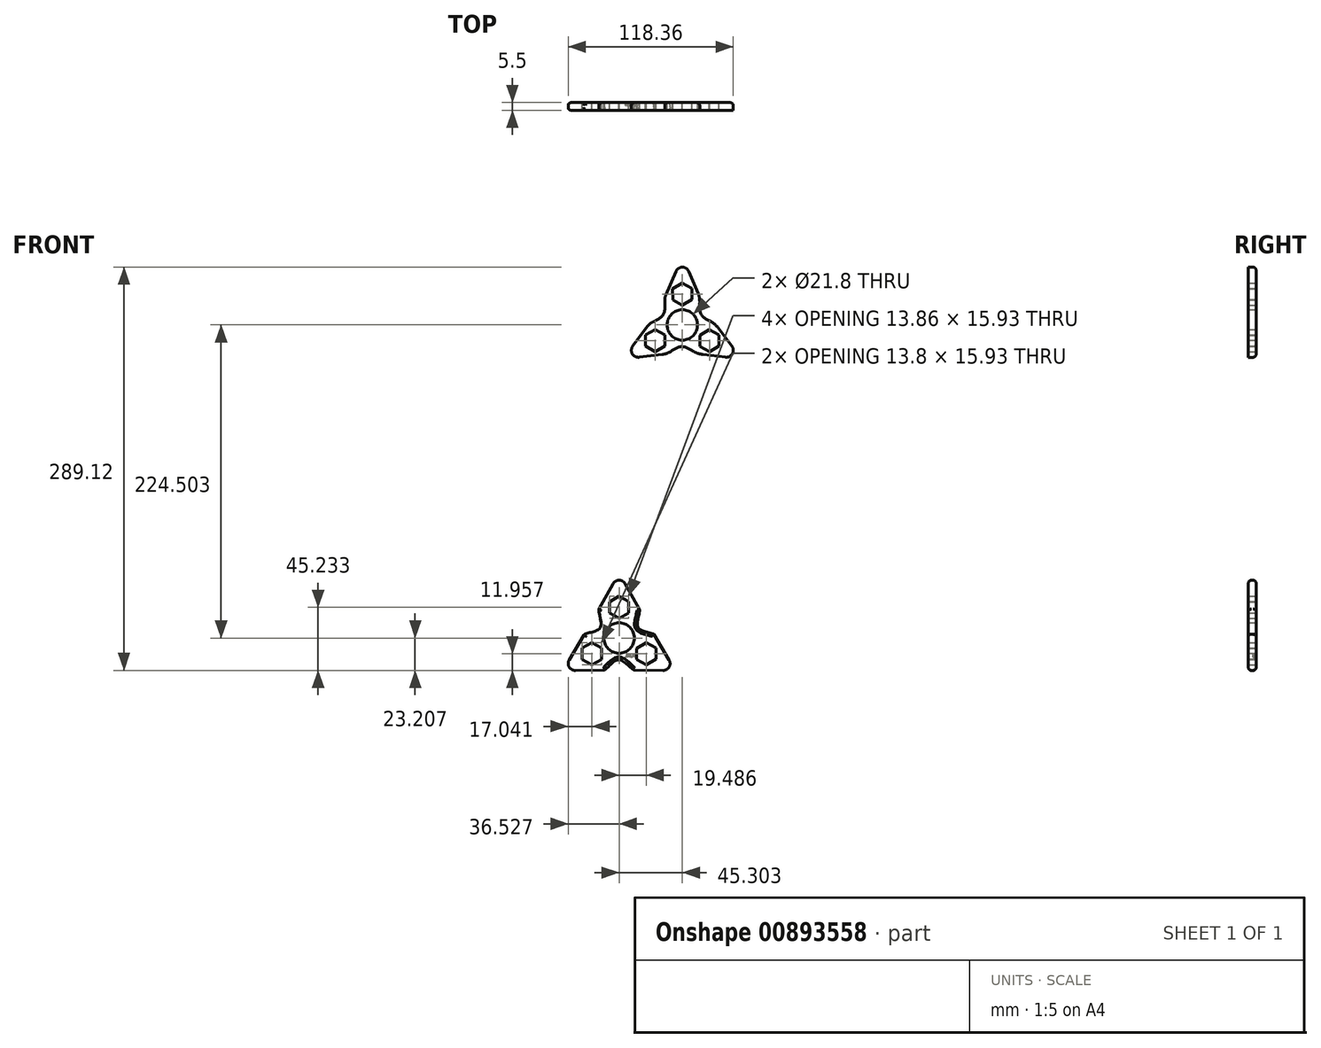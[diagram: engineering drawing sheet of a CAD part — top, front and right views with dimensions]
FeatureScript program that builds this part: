
annotation { "Feature Type Name" : "Feature", "Feature Type Description" : "" }
export const myFeature = defineFeature(function(context is Context, id is Id, definition is map)
    precondition{}
    {
        {
            var Q0;
            Q0=qCreatedBy(makeId("Front.planeOp"),FACE);
            var sketch = newSketch(context, id + "F0", { "sketchPlane" : qUnion([Q0])});
            skCircle(sketch, "E0", {"center": v(0, 0) * mm, "radius": 10.9 * mm});
            skCircle(sketch, "E1.cCircle", {"center": v(0, 22.03) * mm, "radius": 6.9 * mm, "construction": true});
            skLineSegment(sketch, "E1.0", {"start": v(0.06, 14.06) * mm, "end": v(-6.87, 17.99) * mm});
            skLineSegment(sketch, "E1.1", {"start": v(-6.87, 17.99) * mm, "end": v(-6.93, 25.96) * mm});
            skLineSegment(sketch, "E1.2", {"start": v(-6.93, 25.96) * mm, "end": v(-0.06, 30) * mm});
            skLineSegment(sketch, "E1.3", {"start": v(-0.06, 30) * mm, "end": v(6.87, 26.06) * mm});
            skLineSegment(sketch, "E1.4", {"start": v(6.87, 26.06) * mm, "end": v(6.93, 18.1) * mm});
            skLineSegment(sketch, "E1.5", {"start": v(6.93, 18.1) * mm, "end": v(0.06, 14.06) * mm});
            skLineSegment(sketch, "E2", {"start": v(0, 10.9) * mm, "end": v(0.06, 14.06) * mm});
            skCircle(sketch, "E3.cCircle", {"center": v(-19.49, -11.25) * mm, "radius": 6.9 * mm, "construction": true});
            skLineSegment(sketch, "E3.0", {"start": v(-26.39, -15.23) * mm, "end": v(-26.39, -7.27) * mm});
            skLineSegment(sketch, "E3.1", {"start": v(-26.39, -7.27) * mm, "end": v(-19.49, -3.28) * mm});
            skLineSegment(sketch, "E3.2", {"start": v(-19.49, -3.28) * mm, "end": v(-12.59, -7.27) * mm});
            skLineSegment(sketch, "E3.3", {"start": v(-12.59, -7.27) * mm, "end": v(-12.59, -15.23) * mm});
            skLineSegment(sketch, "E3.4", {"start": v(-12.59, -15.23) * mm, "end": v(-19.49, -19.22) * mm});
            skLineSegment(sketch, "E3.5", {"start": v(-19.49, -19.22) * mm, "end": v(-26.39, -15.23) * mm});
            skPoint(sketch, "E3.0.midPoint", {"position": v(-26.39, -11.25) * mm});
            skCircle(sketch, "E4.cCircle", {"center": v(19.49, -11.25) * mm, "radius": 6.9 * mm, "construction": true});
            skLineSegment(sketch, "E4.0", {"start": v(19.42, -3.28) * mm, "end": v(26.35, -7.21) * mm});
            skLineSegment(sketch, "E4.1", {"start": v(26.35, -7.21) * mm, "end": v(26.42, -15.18) * mm});
            skLineSegment(sketch, "E4.2", {"start": v(26.42, -15.18) * mm, "end": v(19.55, -19.22) * mm});
            skLineSegment(sketch, "E4.3", {"start": v(19.55, -19.22) * mm, "end": v(12.62, -15.29) * mm});
            skLineSegment(sketch, "E4.4", {"start": v(12.62, -15.29) * mm, "end": v(12.56, -7.32) * mm});
            skLineSegment(sketch, "E4.5", {"start": v(12.56, -7.32) * mm, "end": v(19.42, -3.28) * mm});
            skPoint(sketch, "E4.0.midPoint", {"position": v(22.89, -5.25) * mm});
            skLineSegment(sketch, "E5", {"start": v(-12.76, 19.17) * mm, "end": v(-4.6, 38.37) * mm});
            skLineSegment(sketch, "E6.MirrorCS", {"start": v(12.76, 19.17) * mm, "end": v(4.6, 38.37) * mm});
            skLineSegment(sketch, "E7.MirrorCS", {"start": v(-10.22, -20.64) * mm, "end": v(-30.92, -23.17) * mm});
            skLineSegment(sketch, "E8.MirrorCS", {"start": v(-22.99, 1.46) * mm, "end": v(-35.53, -15.2) * mm});
            skLineSegment(sketch, "E9.MirrorCS", {"start": v(22.99, 1.46) * mm, "end": v(35.53, -15.2) * mm});
            skLineSegment(sketch, "E10.MirrorCS", {"start": v(10.22, -20.64) * mm, "end": v(30.92, -23.17) * mm});
            skFitSpline(sketch, "E11", {"points": [v(-22.99, 1.46) * mm, v(-13.66, 7.37) * mm, v(-12.76, 19.17) * mm], "startDerivative": vector(23.21, 9.28) * mm, "endDerivative": vector(-2.61, 26.04) * mm});
            skFitSpline(sketch, "E12.MirrorCS", {"points": [v(-10.22, -20.64) * mm, v(-0.44, -15.52) * mm, v(10.22, -20.64) * mm], "startDerivative": vector(19.65, 15.46) * mm, "endDerivative": vector(21.24, -15.28) * mm});
            skFitSpline(sketch, "E13.MirrorCS", {"points": [v(22.99, 1.46) * mm, v(13.66, 7.37) * mm, v(12.76, 19.17) * mm], "startDerivative": vector(-23.21, 9.28) * mm, "endDerivative": vector(2.61, 26.04) * mm});
            skPoint(sketch, "E14.visualSharp", {"position": v(0, 49.19) * mm});
            skArc(sketch, "E14.filletArc", {"start": v(4.6, 38.37) * mm, "mid": v(0, 41.4) * mm, "end": v(-4.6, 38.37) * mm});
            skPoint(sketch, "E15.visualSharp", {"position": v(-42.6, -24.6) * mm});
            skArc(sketch, "E15.filletArc", {"start": v(-35.53, -15.2) * mm, "mid": v(-35.86, -20.7) * mm, "end": v(-30.92, -23.17) * mm});
            skPoint(sketch, "E16.visualSharp", {"position": v(42.6, -24.6) * mm});
            skArc(sketch, "E16.filletArc", {"start": v(30.92, -23.17) * mm, "mid": v(35.86, -20.7) * mm, "end": v(35.53, -15.2) * mm});
            skCircle(sketch, "E17", {"center": v(-45.3, -224.5) * mm, "radius": 10.9 * mm});
            skCircle(sketch, "E18.cCircle", {"center": v(-45.3, -202.48) * mm, "radius": 6.9 * mm, "construction": true});
            skLineSegment(sketch, "E18.0", {"start": v(-45.24, -210.44) * mm, "end": v(-52.17, -206.51) * mm});
            skLineSegment(sketch, "E18.1", {"start": v(-52.17, -206.51) * mm, "end": v(-52.23, -198.55) * mm});
            skLineSegment(sketch, "E18.2", {"start": v(-52.23, -198.55) * mm, "end": v(-45.36, -194.5) * mm});
            skLineSegment(sketch, "E18.3", {"start": v(-45.36, -194.5) * mm, "end": v(-38.43, -198.44) * mm});
            skLineSegment(sketch, "E18.4", {"start": v(-38.43, -198.44) * mm, "end": v(-38.37, -206.4) * mm});
            skLineSegment(sketch, "E18.5", {"start": v(-38.37, -206.4) * mm, "end": v(-45.24, -210.44) * mm});
            skCircle(sketch, "E19.cCircle", {"center": v(-64.79, -235.75) * mm, "radius": 6.9 * mm, "construction": true});
            skLineSegment(sketch, "E19.0", {"start": v(-71.69, -239.74) * mm, "end": v(-71.69, -231.77) * mm});
            skLineSegment(sketch, "E19.1", {"start": v(-71.69, -231.77) * mm, "end": v(-64.79, -227.79) * mm});
            skLineSegment(sketch, "E19.2", {"start": v(-64.79, -227.79) * mm, "end": v(-57.89, -231.77) * mm});
            skLineSegment(sketch, "E19.3", {"start": v(-57.89, -231.77) * mm, "end": v(-57.89, -239.74) * mm});
            skLineSegment(sketch, "E19.4", {"start": v(-57.89, -239.74) * mm, "end": v(-64.79, -243.72) * mm});
            skLineSegment(sketch, "E19.5", {"start": v(-64.79, -243.72) * mm, "end": v(-71.69, -239.74) * mm});
            skPoint(sketch, "E19.0.midPoint", {"position": v(-71.69, -235.75) * mm});
            skCircle(sketch, "E20.cCircle", {"center": v(-25.82, -235.75) * mm, "radius": 6.9 * mm, "construction": true});
            skLineSegment(sketch, "E20.0", {"start": v(-25.88, -227.79) * mm, "end": v(-18.95, -231.72) * mm});
            skLineSegment(sketch, "E20.1", {"start": v(-18.95, -231.72) * mm, "end": v(-18.89, -239.68) * mm});
            skLineSegment(sketch, "E20.2", {"start": v(-18.89, -239.68) * mm, "end": v(-25.76, -243.72) * mm});
            skLineSegment(sketch, "E20.3", {"start": v(-25.76, -243.72) * mm, "end": v(-32.69, -239.79) * mm});
            skLineSegment(sketch, "E20.4", {"start": v(-32.69, -239.79) * mm, "end": v(-32.75, -231.82) * mm});
            skLineSegment(sketch, "E20.5", {"start": v(-32.75, -231.82) * mm, "end": v(-25.88, -227.79) * mm});
            skPoint(sketch, "E20.0.midPoint", {"position": v(-22.41, -229.75) * mm});
            skLineSegment(sketch, "E21.MirrorCS", {"start": v(-20.46, -221.76) * mm, "end": v(-9.48, -240.14) * mm});
            skLineSegment(sketch, "E22.MirrorCS", {"start": v(-34.96, -247.4) * mm, "end": v(-13.85, -247.7) * mm});
            skFitSpline(sketch, "E23", {"points": [v(-70.14, -221.76) * mm, v(-58.96, -217.13) * mm, v(-59.95, -204.1) * mm], "startDerivative": vector(23.21, 9.28) * mm, "endDerivative": vector(-2.61, 26.04) * mm});
            skFitSpline(sketch, "E24.MirrorCS", {"points": [v(-55.65, -247.4) * mm, v(-45.75, -240.02) * mm, v(-34.96, -247.4) * mm], "startDerivative": vector(19.65, 15.46) * mm, "endDerivative": vector(21.24, -15.28) * mm});
            skFitSpline(sketch, "E25.MirrorCS", {"points": [v(-20.46, -221.76) * mm, v(-31.64, -217.13) * mm, v(-30.5, -204.36) * mm], "startDerivative": vector(-23.21, 9.28) * mm, "endDerivative": vector(2.61, 26.04) * mm});
            skPoint(sketch, "E26.visualSharp", {"position": v(-45.3, -175.32) * mm});
            skArc(sketch, "E26.filletArc", {"start": v(-40.7, -186.14) * mm, "mid": v(-45.3, -183.1) * mm, "end": v(-49.9, -186.14) * mm});
            skPoint(sketch, "E27.visualSharp", {"position": v(-87.9, -249.1) * mm});
            skArc(sketch, "E27.filletArc", {"start": v(-80.83, -239.7) * mm, "mid": v(-81.16, -245.2) * mm, "end": v(-76.23, -247.67) * mm});
            skPoint(sketch, "E28.visualSharp", {"position": v(-4.88, -247.84) * mm});
            skArc(sketch, "E28.filletArc", {"start": v(-13.85, -247.7) * mm, "mid": v(-9.44, -245.2) * mm, "end": v(-9.48, -240.14) * mm});
            skLineSegment(sketch, "E29.MirrorCS", {"start": v(-70.14, -221.76) * mm, "end": v(-81.13, -240.14) * mm});
            skLineSegment(sketch, "E30.MirrorCS", {"start": v(-55.65, -247.4) * mm, "end": v(-76.76, -247.7) * mm});
            skLineSegment(sketch, "E31.MirrorCS", {"start": v(-59.95, -204.1) * mm, "end": v(-49.67, -185.66) * mm});
            skLineSegment(sketch, "E32.MirrorCS", {"start": v(-30.5, -204.36) * mm, "end": v(-40.94, -185.66) * mm});
            skSolve(sketch);
        }
        {
            var Q0;
            Q0 = qSketchRegion(id + "F0", true);
            extrude(context, id + "F1", {"entities" : qUnion([Q0]), "depth" : 5.5 * mm, "offsetDistance" : 25 * mm});
        }
        {
            var Q0;
            {var subQ0=sQuery(id+"F0.wireOp",EDGE,"E11");var subQ1=sQuery(id+"F0.wireOp",EDGE,"E5");Q0=makeQuery(id+"F1qOhTPMWAMd5Jx_0.boolean.opBoolean","MERGE",EDGE,{"derivedFrom":[makeQuery(id+"F1.opExtrude","SWEPT_EDGE",EDGE,{"disambiguationData":[OSD([subQ1,subQ0])]}),makeQuery(id+"F1qOhTPMWAMd5Jx_0.opExtrude","SWEPT_EDGE",EDGE,{"disambiguationData":[OSD([subQ1,subQ0])]})]});}
            fillet(context, id + "F2", {"entities" : qUnion([Q0]), "radius" : 9.27 * mm, "tangentPropagation" : true, "allowEdgeOverflow" : false});
        }
        {
            var Q0;
            {var subQ0=sQuery(id+"F0.wireOp",EDGE,"E11");var subQ1=sQuery(id+"F0.wireOp",EDGE,"E8.MirrorCS");Q0=makeQuery(id+"F1qOhTPMWAMd5Jx_0.boolean.opBoolean","MERGE",EDGE,{"derivedFrom":[makeQuery(id+"F1.opExtrude","SWEPT_EDGE",EDGE,{"disambiguationData":[OSD([subQ1,subQ0])]}),makeQuery(id+"F1qOhTPMWAMd5Jx_0.opExtrude","SWEPT_EDGE",EDGE,{"disambiguationData":[OSD([subQ1,subQ0])]})]});}
            fillet(context, id + "F3", {"entities" : qUnion([Q0]), "radius" : 10.43 * mm, "tangentPropagation" : true, "allowEdgeOverflow" : false});
        }
        {
            var Q0;
            {var subQ0=sQuery(id+"F0.wireOp",EDGE,"E12.MirrorCS");var subQ1=sQuery(id+"F0.wireOp",EDGE,"E7.MirrorCS");Q0=makeQuery(id+"F1qOhTPMWAMd5Jx_0.boolean.opBoolean","MERGE",EDGE,{"derivedFrom":[makeQuery(id+"F1.opExtrude","SWEPT_EDGE",EDGE,{"disambiguationData":[OSD([subQ1,subQ0])]}),makeQuery(id+"F1qOhTPMWAMd5Jx_0.opExtrude","SWEPT_EDGE",EDGE,{"disambiguationData":[OSD([subQ1,subQ0])]})]});}
            fillet(context, id + "F4", {"entities" : qUnion([Q0]), "radius" : 15.65 * mm, "tangentPropagation" : true, "allowEdgeOverflow" : false});
        }
        {
            var Q0;
            {var subQ0=sQuery(id+"F0.wireOp",EDGE,"E12.MirrorCS");var subQ1=sQuery(id+"F0.wireOp",EDGE,"E10.MirrorCS");Q0=makeQuery(id+"F1qOhTPMWAMd5Jx_0.boolean.opBoolean","MERGE",EDGE,{"derivedFrom":[makeQuery(id+"F1.opExtrude","SWEPT_EDGE",EDGE,{"disambiguationData":[OSD([subQ1,subQ0])]}),makeQuery(id+"F1qOhTPMWAMd5Jx_0.opExtrude","SWEPT_EDGE",EDGE,{"disambiguationData":[OSD([subQ1,subQ0])]})]});}
            fillet(context, id + "F5", {"entities" : qUnion([Q0]), "radius" : 18.54 * mm, "tangentPropagation" : true, "allowEdgeOverflow" : false});
        }
        {
            var Q0;
            {var subQ0=sQuery(id+"F0.wireOp",EDGE,"E13.MirrorCS");var subQ1=sQuery(id+"F0.wireOp",EDGE,"E9.MirrorCS");Q0=makeQuery(id+"F1qOhTPMWAMd5Jx_0.boolean.opBoolean","MERGE",EDGE,{"derivedFrom":[makeQuery(id+"F1.opExtrude","SWEPT_EDGE",EDGE,{"disambiguationData":[OSD([subQ1,subQ0])]}),makeQuery(id+"F1qOhTPMWAMd5Jx_0.opExtrude","SWEPT_EDGE",EDGE,{"disambiguationData":[OSD([subQ1,subQ0])]})]});}
            fillet(context, id + "F6", {"entities" : qUnion([Q0]), "radius" : 18.26 * mm, "tangentPropagation" : true, "allowEdgeOverflow" : false});
        }
        {
            var Q0;
            {var subQ0=sQuery(id+"F0.wireOp",EDGE,"E13.MirrorCS");var subQ1=sQuery(id+"F0.wireOp",EDGE,"E6.MirrorCS");Q0=makeQuery(id+"F1qOhTPMWAMd5Jx_0.boolean.opBoolean","MERGE",EDGE,{"derivedFrom":[makeQuery(id+"F1.opExtrude","SWEPT_EDGE",EDGE,{"disambiguationData":[OSD([subQ1,subQ0])]}),makeQuery(id+"F1qOhTPMWAMd5Jx_0.opExtrude","SWEPT_EDGE",EDGE,{"disambiguationData":[OSD([subQ1,subQ0])]})]});}
            fillet(context, id + "F7", {"entities" : qUnion([Q0]), "radius" : 15.45 * mm, "tangentPropagation" : true, "allowEdgeOverflow" : false});
        }
        {
            var Q0;
            Q0=makeQuery(id+"F1.opExtrude","CAP_EDGE",EDGE,{"disambiguationData":[OSD([sQuery(id+"F0.wireOp",EDGE,"E5")])],"isStart":true});
            fillet(context, id + "F8", {"entities" : qUnion([Q0]), "radius" : 2.17 * mm, "tangentPropagation" : true, "allowEdgeOverflow" : false});
        }
        {
            var Q0;
            Q0=makeQuery(id+"F1.opExtrude","CAP_EDGE",EDGE,{"disambiguationData":[OSD([sQuery(id+"F0.wireOp",EDGE,"E23")])],"isStart":true});
            var Q1;
            Q1=makeQuery(id+"F1.opExtrude","CAP_EDGE",EDGE,{"disambiguationData":[OSD([sQuery(id+"F0.wireOp",EDGE,"E31.MirrorCS")])],"isStart":true});
            var Q2;
            Q2=makeQuery(id+"F1.opExtrude","CAP_EDGE",EDGE,{"disambiguationData":[OSD([sQuery(id+"F0.wireOp",EDGE,"E25.MirrorCS")])],"isStart":true});
            var Q3;
            Q3=makeQuery(id+"F1.opExtrude","CAP_EDGE",EDGE,{"disambiguationData":[OSD([sQuery(id+"F0.wireOp",EDGE,"E21.MirrorCS")])],"isStart":true});
            var Q4;
            Q4=makeQuery(id+"F1.opExtrude","CAP_EDGE",EDGE,{"disambiguationData":[OSD([sQuery(id+"F0.wireOp",EDGE,"E24.MirrorCS")])],"isStart":true});
            var Q5;
            Q5=makeQuery(id+"F1.opExtrude","CAP_EDGE",EDGE,{"disambiguationData":[OSD([sQuery(id+"F0.wireOp",EDGE,"E30.MirrorCS")])],"isStart":true});
            fillet(context, id + "F9", {"entities" : qUnion([Q0, Q1, Q2, Q3, Q4, Q5]), "radius" : 2 * mm, "tangentPropagation" : true, "allowEdgeOverflow" : false});
        }
        {
            var Q0;
            Q0=makeQuery(id+"F1.opExtrude","CAP_EDGE",EDGE,{"disambiguationData":[OSD([sQuery(id+"F0.wireOp",EDGE,"E24.MirrorCS")])],"isStart":false});
            var Q1;
            Q1=makeQuery(id+"F1.opExtrude","CAP_EDGE",EDGE,{"disambiguationData":[OSD([sQuery(id+"F0.wireOp",EDGE,"E30.MirrorCS")])],"isStart":false});
            fillet(context, id + "F10", {"entities" : qUnion([Q0, Q1]), "radius" : 2 * mm, "tangentPropagation" : true, "allowEdgeOverflow" : false});
        }
        {
            var Q0;
            Q0=makeQuery(id+"F1.opExtrude","CAP_EDGE",EDGE,{"disambiguationData":[OSD([sQuery(id+"F0.wireOp",EDGE,"E23")])],"isStart":false});
            fillet(context, id + "F11", {"entities" : qUnion([Q0]), "radius" : 2 * mm, "tangentPropagation" : true, "allowEdgeOverflow" : false});
        }
        {
            var Q0;
            Q0=makeQuery(id+"F1.opExtrude","CAP_EDGE",EDGE,{"disambiguationData":[OSD([sQuery(id+"F0.wireOp",EDGE,"E31.MirrorCS")])],"isStart":false});
            fillet(context, id + "F12", {"entities" : qUnion([Q0]), "radius" : 2 * mm, "tangentPropagation" : true, "allowEdgeOverflow" : false});
        }
        {
            var Q0;
            Q0=makeQuery(id+"F1.opExtrude","CAP_EDGE",EDGE,{"disambiguationData":[OSD([sQuery(id+"F0.wireOp",EDGE,"E25.MirrorCS")])],"isStart":false});
            var Q1;
            Q1=makeQuery(id+"F1.opExtrude","CAP_EDGE",EDGE,{"disambiguationData":[OSD([sQuery(id+"F0.wireOp",EDGE,"E21.MirrorCS")])],"isStart":false});
            fillet(context, id + "F13", {"entities" : qUnion([Q0, Q1]), "radius" : 2 * mm, "tangentPropagation" : true, "allowEdgeOverflow" : false});
        }
        {
            var Q0;
            Q0=qCreatedBy(makeId("Front.planeOp"),FACE);
            var sketch = newSketch(context, id + "F14", { "sketchPlane" : qUnion([Q0])});
            skText(sketch, "E33", { "text": ".M.A", "fontName": "OpenSans-Regular.ttf"});
            const initialGuessF14  = {"E33": [-0.041, -0.23833, 1, 0, 0.00253]};
            skSetInitialGuess(sketch, initialGuessF14);
            skSolve(sketch);
        }
        {
            var Q0;
            Q0 = qSketchRegion(id + "F14", true);
            extrude(context, id + "F15", {"entities" : qUnion([Q0]), "operationType" : NewBodyOperationType.REMOVE, "depth" : 2 * mm, "offsetDistance" : 25 * mm});
        }
    });
